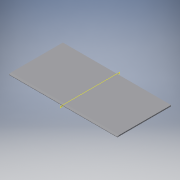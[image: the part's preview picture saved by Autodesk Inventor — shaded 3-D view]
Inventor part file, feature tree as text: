
AUTODESK INVENTOR PART (.ipt)
format: ipt  version: 2017 (Build 210142000, 142)  size: 102,912 bytes
history: native  units: mm
features: fillet x2, extrude x1, sketch x1
ambient origin geometry x8: Origin, YZ Plane, XZ Plane, XY Plane, X Axis, Y Axis, Z Axis, Center Point
bodies: Volumenkörper1 (feature_tree)
feature tree (4):
  extrude  "Extrusion1"  Depth=6.0mm
  fillet  "Rundung1"  Radius=40.0mm
  fillet  "Rundung2"  Radius=10.0mm
  sketch  "Skizze1"  dims[d0=20.0mm d1=1000.0mm d2=40.0mm d3=10.0mm d4=2000.0mm d5=0.0mm d6=100.0mm d7=6.0mm]
